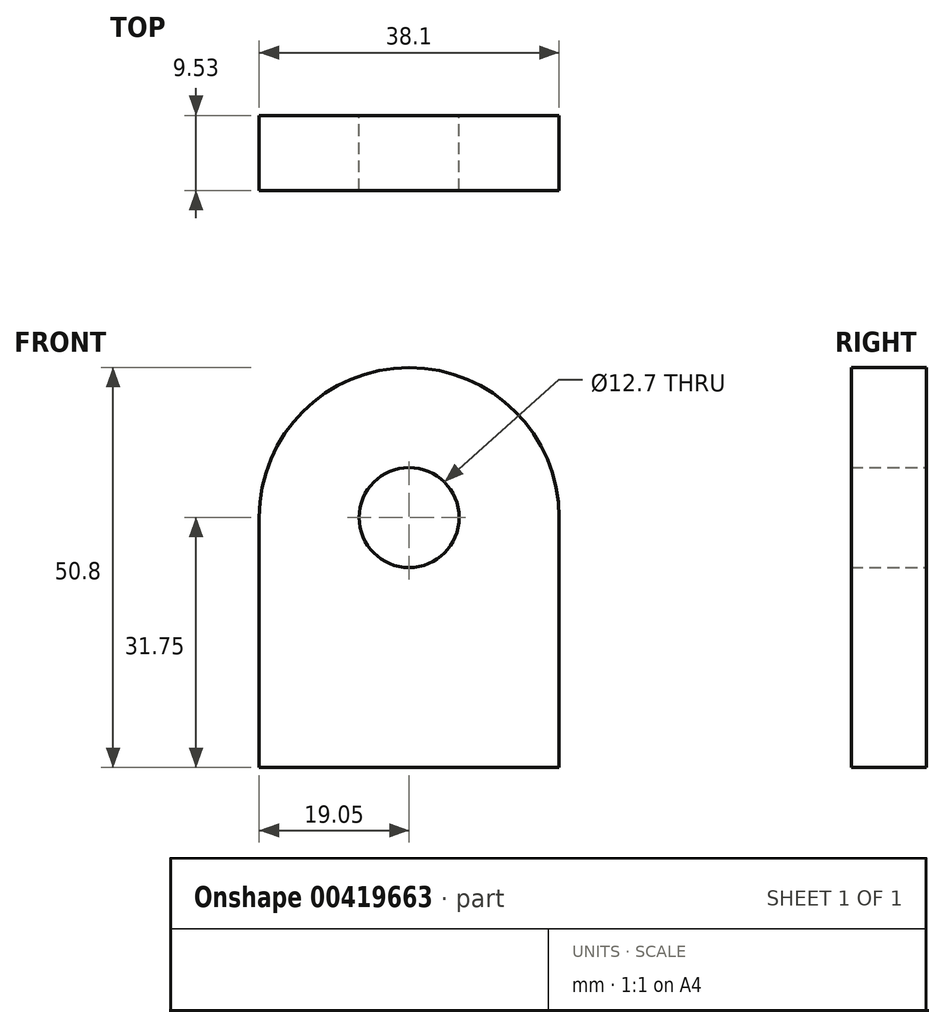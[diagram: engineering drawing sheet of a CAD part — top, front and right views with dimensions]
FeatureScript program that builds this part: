
annotation { "Feature Type Name" : "Feature", "Feature Type Description" : "" }
export const myFeature = defineFeature(function(context is Context, id is Id, definition is map)
    precondition{}
    {
        {
            var Q0;
            Q0=qCreatedBy(makeId("Front.planeOp"),FACE);
            var sketch = newSketch(context, id + "F0", { "sketchPlane" : qUnion([Q0])});
            skCircle(sketch, "E0", {"center": v(0, 0) * mm, "radius": 6.35 * mm});
            skArc(sketch, "E1", {"start": v(19.05, 0) * mm, "mid": v(0, 19.05) * mm, "end": v(-19.05, 0) * mm});
            skLineSegment(sketch, "E2", {"start": v(-19.05, 0) * mm, "end": v(-19.05, -31.75) * mm});
            skLineSegment(sketch, "E3.MirrorCS", {"start": v(19.05, 0) * mm, "end": v(19.05, -31.75) * mm});
            skLineSegment(sketch, "E4", {"start": v(19.05, -31.75) * mm, "end": v(-19.05, -31.75) * mm});
            skSolve(sketch);
        }
        {
            var Q0;
            Q0=makeQuery(id+"F0.imprint","IMPRINT",FACE,{"disambiguationData":[TD([[makeQuery(id+"F0.imprint","IMPRINT",EDGE,{"derivedFrom":sQuery(id+"F0.wireOp",EDGE,"E0")}),-1.0]])]});
            extrude(context, id + "F1", {"entities" : qUnion([Q0]), "depth" : 9.52 * mm});
        }
    });
